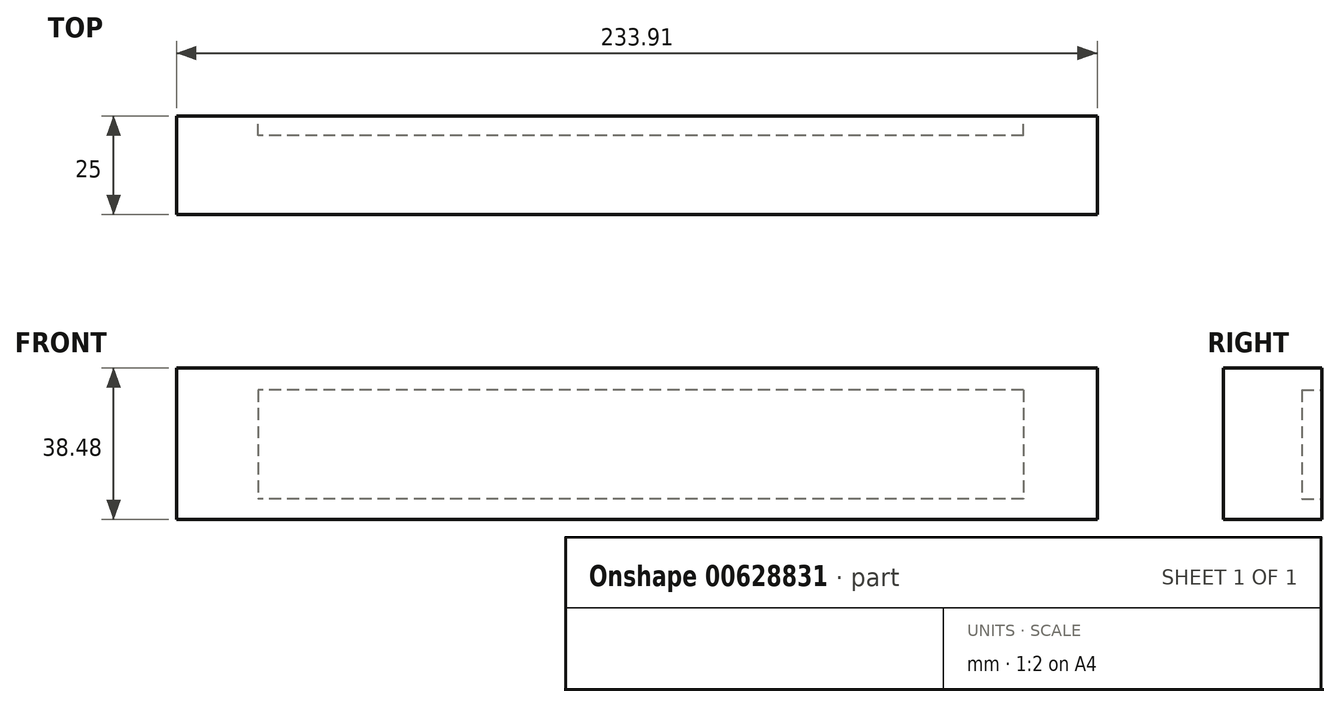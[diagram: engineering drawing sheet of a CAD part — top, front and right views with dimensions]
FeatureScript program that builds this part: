
annotation { "Feature Type Name" : "Feature", "Feature Type Description" : "" }
export const myFeature = defineFeature(function(context is Context, id is Id, definition is map)
    precondition{}
    {
        {
            var Q0;
            Q0=qCreatedBy(makeId("Front.planeOp"),FACE);
            var sketch = newSketch(context, id + "F0", { "sketchPlane" : qUnion([Q0])});
            skFitSpline(sketch, "E0", {"points": [v(-117.43, 0) * mm, v(-40.31, 40.47) * mm, v(53.38, 41.7) * mm, v(116.48, 0) * mm], "startDerivative": vector(214.01, 141.38) * mm, "endDerivative": vector(181.48, -159.93) * mm});
            skSolve(sketch);
        }
        {
            var Q0;
            Q0=qCreatedBy(makeId("Right.planeOp"),FACE);
            var sketch = newSketch(context, id + "F1", { "sketchPlane" : qUnion([Q0])});
            skCircle(sketch, "E1", {"center": v(0, 0) * mm, "radius": 13.81 * mm});
            skSolve(sketch);
        }
        {
            var Q0;
            Q0=qCreatedBy(makeId("Front.planeOp"),FACE);
            var sketch = newSketch(context, id + "F2", { "sketchPlane" : qUnion([Q0])});
            skLineSegment(sketch, "E2.bottom", {"start": v(116.48, -40.89) * mm, "end": v(-117.43, -40.89) * mm});
            skLineSegment(sketch, "E2.top", {"start": v(116.48, -79.37) * mm, "end": v(-117.43, -79.37) * mm});
            skLineSegment(sketch, "E2.left", {"start": v(116.48, -40.89) * mm, "end": v(116.48, -79.37) * mm});
            skLineSegment(sketch, "E2.right", {"start": v(-117.43, -40.89) * mm, "end": v(-117.43, -79.37) * mm});
            skSolve(sketch);
        }
        {
            var Q0;
            Q0=makeQuery(id+"F2.imprint","IMPRINT",FACE,{"disambiguationData":[TD([[makeQuery(id+"F2.imprint","IMPRINT",EDGE,{"derivedFrom":sQuery(id+"F2.wireOp",EDGE,"E2.bottom")}),1.0]])]});
            extrude(context, id + "F3", {"entities" : qUnion([Q0]), "endBound" : BoundingType.SYMMETRIC, "depth" : 25 * mm, "offsetDistance" : 25 * mm});
        }
        {
            var Q0;
            Q0=makeQuery(id+"F3.opExtrude","CAP_FACE",FACE,{"disambiguationData":[OSD([sQuery(id+"F2.wireOp",EDGE,"E2.bottom"),sQuery(id+"F2.wireOp",EDGE,"E2.top"),sQuery(id+"F2.wireOp",EDGE,"E2.left"),sQuery(id+"F2.wireOp",EDGE,"E2.right")])],"isStart":true});
            var sketch = newSketch(context, id + "F4", { "sketchPlane" : qUnion([Q0])});
            skLineSegment(sketch, "E3.bottom", {"start": v(-97.7, -46.49) * mm, "end": v(96.76, -46.49) * mm});
            skLineSegment(sketch, "E3.top", {"start": v(-97.7, -74.1) * mm, "end": v(96.76, -74.1) * mm});
            skLineSegment(sketch, "E3.left", {"start": v(-97.7, -46.49) * mm, "end": v(-97.7, -74.1) * mm});
            skLineSegment(sketch, "E3.right", {"start": v(96.76, -46.49) * mm, "end": v(96.76, -74.1) * mm});
            skSolve(sketch);
        }
        {
            var Q0;
            Q0=makeQuery(id+"F4.imprint","IMPRINT",FACE,{"disambiguationData":[TD([[makeQuery(id+"F4.imprint","IMPRINT",EDGE,{"derivedFrom":sQuery(id+"F4.wireOp",EDGE,"E3.bottom")}),-1.0]])]});
            extrude(context, id + "F5", {"entities" : qUnion([Q0]), "operationType" : NewBodyOperationType.REMOVE, "oppositeDirection" : true, "depth" : 5 * mm, "offsetDistance" : 25 * mm});
        }
    });
